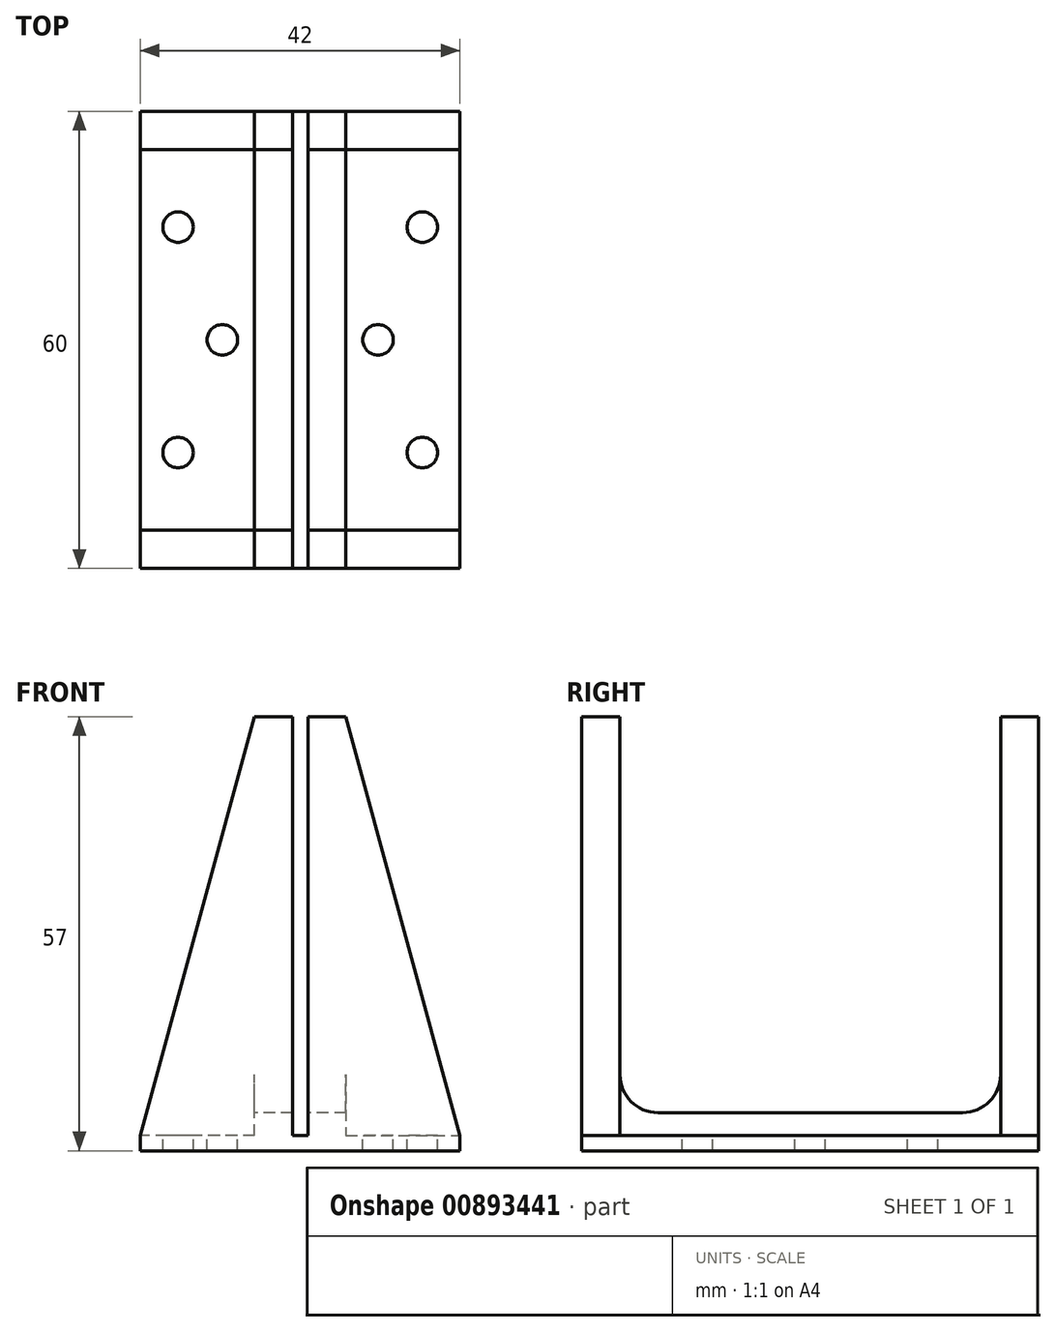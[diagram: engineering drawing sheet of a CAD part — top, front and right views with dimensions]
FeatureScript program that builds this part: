
annotation { "Feature Type Name" : "Feature", "Feature Type Description" : "" }
export const myFeature = defineFeature(function(context is Context, id is Id, definition is map)
    precondition{}
    {
        {
            var Q0;
            Q0=qCreatedBy(makeId("Front.planeOp"),FACE);
            var sketch = newSketch(context, id + "F0", { "sketchPlane" : qUnion([Q0])});
            skLineSegment(sketch, "E0", {"start": v(0, 0) * mm, "end": v(0, 55) * mm});
            skLineSegment(sketch, "E1", {"start": v(0, 55) * mm, "end": v(5, 55) * mm});
            skLineSegment(sketch, "E2", {"start": v(5, 55) * mm, "end": v(5, 0) * mm});
            skLineSegment(sketch, "E3", {"start": v(5, 0) * mm, "end": v(7, 0) * mm});
            skLineSegment(sketch, "E4", {"start": v(7, 0) * mm, "end": v(7, 55) * mm});
            skLineSegment(sketch, "E5", {"start": v(7, 55) * mm, "end": v(12, 55) * mm});
            skLineSegment(sketch, "E6", {"start": v(12, 55) * mm, "end": v(12, 0) * mm});
            skLineSegment(sketch, "E7", {"start": v(12, 0) * mm, "end": v(27, 0) * mm});
            skLineSegment(sketch, "E8", {"start": v(27, 0) * mm, "end": v(27, -2) * mm});
            skLineSegment(sketch, "E9", {"start": v(0, 0) * mm, "end": v(-15, 0) * mm});
            skLineSegment(sketch, "E10", {"start": v(-15, 0) * mm, "end": v(-15, -2) * mm});
            skLineSegment(sketch, "E11", {"start": v(-15, -2) * mm, "end": v(27, -2) * mm});
            skSolve(sketch);
        }
        {
            var Q0;
            {var subQ0=sQuery(id+"F0.wireOp",EDGE,"E3");Q0=makeQuery(id+"F0.imprint","IMPRINT",FACE,{"disambiguationData":[TD([[makeQuery(id+"F0.imprint","IMPRINT",EDGE,{"derivedFrom":subQ0}),-1.0]])]});}
            extrude(context, id + "F1", {"entities" : qUnion([Q0]), "depth" : 60 * mm, "offsetDistance" : 25 * mm});
        }
        {
            var Q0;
            Q0=makeQuery(id+"F1.opExtrude","SWEPT_FACE",FACE,{"disambiguationData":[OSD([sQuery(id+"F0.wireOp",EDGE,"E0")])]});
            var sketch = newSketch(context, id + "F2", { "sketchPlane" : qUnion([Q0])});
            skLineSegment(sketch, "E12.bottom", {"start": v(5, 55) * mm, "end": v(55, 55) * mm});
            skLineSegment(sketch, "E12.top", {"start": v(10, 3) * mm, "end": v(50, 3) * mm});
            skLineSegment(sketch, "E12.left", {"start": v(5, 55) * mm, "end": v(5, 8) * mm});
            skLineSegment(sketch, "E12.right", {"start": v(55, 55) * mm, "end": v(55, 8) * mm});
            skPoint(sketch, "E13.visualSharp", {"position": v(5, 3) * mm});
            skArc(sketch, "E13.filletArc", {"start": v(5, 8) * mm, "mid": v(6.46, 4.46) * mm, "end": v(10, 3) * mm});
            skPoint(sketch, "E14.visualSharp", {"position": v(55, 3) * mm});
            skArc(sketch, "E14.filletArc", {"start": v(50, 3) * mm, "mid": v(53.54, 4.46) * mm, "end": v(55, 8) * mm});
            skSolve(sketch);
        }
        {
            var Q0;
            Q0=makeQuery(id+"F2.imprint","IMPRINT",FACE,{"disambiguationData":[TD([[makeQuery(id+"F2.imprint","IMPRINT",EDGE,{"derivedFrom":sQuery(id+"F2.wireOp",EDGE,"E12.bottom")}),1.0]])]});
            extrude(context, id + "F3", {"entities" : qUnion([Q0]), "operationType" : NewBodyOperationType.REMOVE, "endBound" : BoundingType.THROUGH_ALL, "oppositeDirection" : true, "depth" : 3.5 * mm, "offsetDistance" : 25 * mm});
        }
        {
            var Q0;
            Q0=makeQuery(id+"F1.opExtrude","SWEPT_FACE",FACE,{"disambiguationData":[OSD([sQuery(id+"F0.wireOp",EDGE,"E9")])]});
            var sketch = newSketch(context, id + "F4", { "sketchPlane" : qUnion([Q0])});
            skLineSegment(sketch, "E15", {"start": v(-10.05, 0) * mm, "end": v(-10.05, -60) * mm, "construction": true});
            skLineSegment(sketch, "E16", {"start": v(-4.22, -60) * mm, "end": v(-4.22, 0) * mm, "construction": true});
            skCircle(sketch, "E17", {"center": v(-10.05, -15.2) * mm, "radius": 2 * mm});
            skCircle(sketch, "E18", {"center": v(-10.05, -44.8) * mm, "radius": 2 * mm});
            skCircle(sketch, "E19", {"center": v(-4.22, -30) * mm, "radius": 2 * mm});
            skPoint(sketch, "E20.0", {"position": v(6, 0) * mm});
            skLineSegment(sketch, "E21", {"start": v(6, 0) * mm, "end": v(6, -60.07) * mm, "construction": true});
            skCircle(sketch, "E22.MirrorC", {"center": v(16.22, -30) * mm, "radius": 2 * mm});
            skLineSegment(sketch, "E23.MirrorCS", {"start": v(16.22, -60) * mm, "end": v(16.22, 0) * mm, "construction": true});
            skLineSegment(sketch, "E24.MirrorCS", {"start": v(22.05, 0) * mm, "end": v(22.05, -60) * mm, "construction": true});
            skCircle(sketch, "E25.MirrorC", {"center": v(22.05, -44.8) * mm, "radius": 2 * mm});
            skCircle(sketch, "E26.MirrorC", {"center": v(22.05, -15.2) * mm, "radius": 2 * mm});
            skSolve(sketch);
        }
        {
            var Q0;
            Q0 = qSketchRegion(id + "F4", true);
            extrude(context, id + "F5", {"entities" : qUnion([Q0]), "operationType" : NewBodyOperationType.REMOVE, "oppositeDirection" : true, "depth" : 25 * mm, "offsetDistance" : 25 * mm});
        }
        {
            var Q0;
            Q0=makeQuery(id+"F1.opExtrude","CAP_FACE",FACE,{"disambiguationData":[OSD([sQuery(id+"F0.wireOp",EDGE,"E0"),sQuery(id+"F0.wireOp",EDGE,"E1"),sQuery(id+"F0.wireOp",EDGE,"E2"),sQuery(id+"F0.wireOp",EDGE,"E3"),sQuery(id+"F0.wireOp",EDGE,"E4"),sQuery(id+"F0.wireOp",EDGE,"E5"),sQuery(id+"F0.wireOp",EDGE,"E6"),sQuery(id+"F0.wireOp",EDGE,"E7"),sQuery(id+"F0.wireOp",EDGE,"E8"),sQuery(id+"F0.wireOp",EDGE,"E9"),sQuery(id+"F0.wireOp",EDGE,"E10"),sQuery(id+"F0.wireOp",EDGE,"E11")])],"isStart":false});
            var sketch = newSketch(context, id + "F6", { "sketchPlane" : qUnion([Q0])});
            skLineSegment(sketch, "E27.0", {"start": v(12, 55) * mm, "end": v(12, 0) * mm});
            skLineSegment(sketch, "E27.1", {"start": v(12, 0) * mm, "end": v(27, 0) * mm});
            skLineSegment(sketch, "E27.2", {"start": v(0, 0) * mm, "end": v(-15, 0) * mm});
            skLineSegment(sketch, "E27.3", {"start": v(0, 0) * mm, "end": v(0, 55) * mm});
            skPoint(sketch, "E27.4", {"position": v(-7.5, 0) * mm});
            skLineSegment(sketch, "E28", {"start": v(0, 55) * mm, "end": v(-15, 0) * mm});
            skLineSegment(sketch, "E29", {"start": v(27, 0) * mm, "end": v(12, 55) * mm});
            skSolve(sketch);
        }
        {
            var Q0;
            Q0=makeQuery(id+"F6.imprint","IMPRINT",FACE,{"disambiguationData":[TD([[makeQuery(id+"F6.imprint","IMPRINT",EDGE,{"derivedFrom":sQuery(id+"F6.wireOp",EDGE,"E27.2")}),-1.0]])]});
            var Q1;
            Q1=makeQuery(id+"F6.imprint","IMPRINT",FACE,{"disambiguationData":[TD([[makeQuery(id+"F6.imprint","IMPRINT",EDGE,{"derivedFrom":sQuery(id+"F6.wireOp",EDGE,"E27.0")}),1.0]])]});
            var Q2;
            Q2=makeQuery(id+"F3.boolean.opBoolean","COPY",FACE,{"disambiguationData":[TD([makeQuery(id+"F1.opExtrude","SWEPT_FACE",FACE,{"disambiguationData":[OSD([sQuery(id+"F0.wireOp",EDGE,"E0")])]})])],"derivedFrom":makeQuery(id+"F3.opExtrude","SWEPT_FACE",FACE,{"disambiguationData":[OSD([sQuery(id+"F2.wireOp",EDGE,"E12.right")])]})});
            extrude(context, id + "F7", {"entities" : qUnion([Q0, Q1]), "endBound" : BoundingType.UP_TO_SURFACE, "oppositeDirection" : true, "depth" : 2 * mm, "endBoundEntityFace" : qUnion([Q2]), "offsetDistance" : 25 * mm});
        }
        {
            var Q0;
            Q0=makeQuery(id+"F7.boolean.opBoolean","SPLIT",EDGE,{"derivedFrom":makeQuery(id+"F1.opExtrude","SWEPT_EDGE",EDGE,{"disambiguationData":[OSD([sQuery(id+"F0.wireOp",EDGE,"E7"),sQuery(id+"F0.wireOp",EDGE,"E8")])]})});
            cPoint(context, id + "F8", {"entities" : qUnion([Q0]), "parameter" : 0.5});
        }
        {
            var Q0;
            Q0=qCreatedBy(makeId("Front.planeOp"),FACE);
            var Q1;
            Q1 = qCreatedBy(id + "F8" ,VERTEX);
            cPlane(context, id + "F9", {"entities" : qUnion([Q0, Q1]), "cplaneType" : CPlaneType.PLANE_POINT, "offset" : 25 * mm, "width" : 150 * mm, "height" : 150 * mm});
        }
        {
            var Q0;
            Q0=makeQuery(id+"F7.opExtrude","SWEPT_BODY",BODY,{"disambiguationData":[OSD([sQuery(id+"F6.wireOp",EDGE,"E27.0"),sQuery(id+"F6.wireOp",EDGE,"E27.1"),sQuery(id+"F6.wireOp",EDGE,"E29")])]});
            var Q1;
            Q1=makeQuery(id+"F7.opExtrude","SWEPT_BODY",BODY,{"disambiguationData":[OSD([sQuery(id+"F6.wireOp",EDGE,"E27.2"),sQuery(id+"F6.wireOp",EDGE,"E27.3"),sQuery(id+"F6.wireOp",EDGE,"E28")])]});
            var Q2;
            Q2=qCreatedBy(id+"F9.planeOp",FACE);
            mirror(context, id + "F10", {"operationType" : NewBodyOperationType.ADD, "entities" : qUnion([Q0, Q1]), "mirrorPlane" : qUnion([Q2])});
        }
    });
